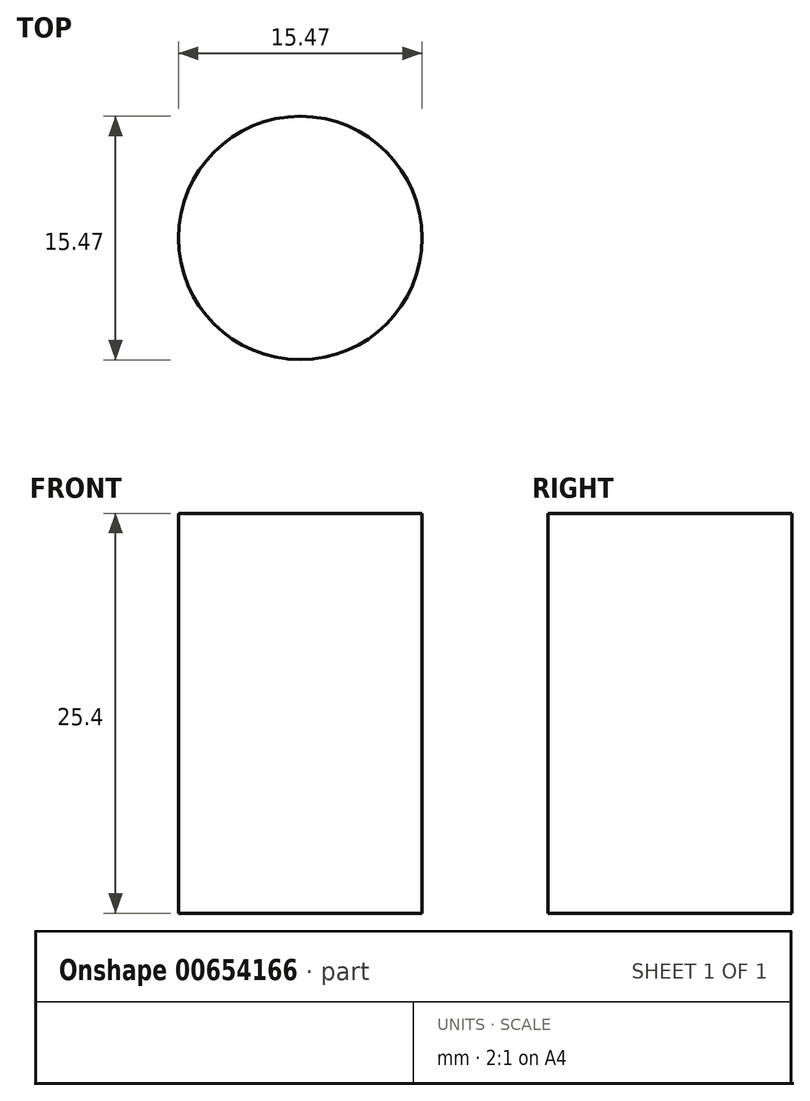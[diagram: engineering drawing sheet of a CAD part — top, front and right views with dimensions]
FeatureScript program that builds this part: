
annotation { "Feature Type Name" : "Feature", "Feature Type Description" : "" }
export const myFeature = defineFeature(function(context is Context, id is Id, definition is map)
    precondition{}
    {
        {
            var Q0;
            Q0=qCreatedBy(makeId("Top.planeOp"),FACE);
            var sketch = newSketch(context, id + "F0", { "sketchPlane" : qUnion([Q0])});
            skCircle(sketch, "E0", {"center": v(47.21, 4.64) * mm, "radius": 7.73 * mm});
            skSolve(sketch);
        }
        {
            var Q0;
            Q0=sQuery(id+"F0.wireOp",EDGE,"E0");
            extrude(context, id + "F1", {"bodyType" : ToolBodyType.SURFACE, "surfaceEntities" : qUnion([Q0]), "depth" : 25.4 * mm, "offsetDistance" : 25.4 * mm});
        }
    });
